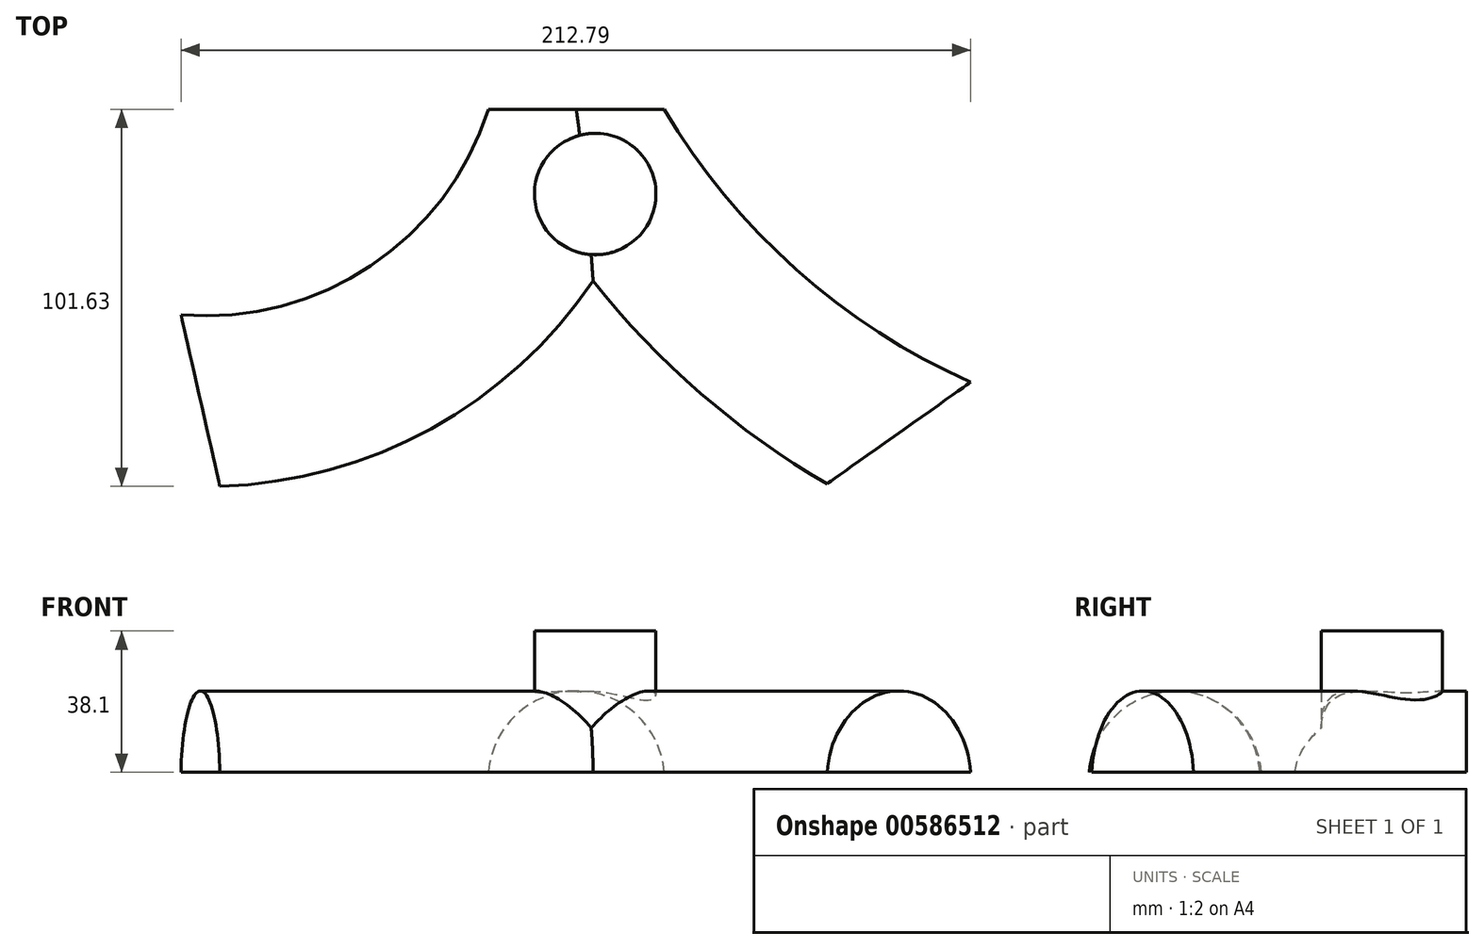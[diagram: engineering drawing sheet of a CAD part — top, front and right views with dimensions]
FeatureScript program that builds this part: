
annotation { "Feature Type Name" : "Feature", "Feature Type Description" : "" }
export const myFeature = defineFeature(function(context is Context, id is Id, definition is map)
    precondition{}
    {
        {
            var Q0;
            Q0=qCreatedBy(makeId("Front.planeOp"),FACE);
            var sketch = newSketch(context, id + "F0", { "sketchPlane" : qUnion([Q0])});
            skArc(sketch, "E0", {"start": v(22.83, 0) * mm, "mid": v(-0.87, 21.9) * mm, "end": v(-24.57, 0) * mm});
            skLineSegment(sketch, "E1", {"start": v(-24.57, 0) * mm, "end": v(22.83, 0) * mm});
            skSolve(sketch);
        }
        {
            var Q0;
            Q0=qCreatedBy(makeId("Top.planeOp"),FACE);
            var sketch = newSketch(context, id + "F1", { "sketchPlane" : qUnion([Q0])});
            skArc(sketch, "E2", {"start": v(-101.98, -79.36) * mm, "mid": v(-37.09, -57.54) * mm, "end": v(0, 0) * mm});
            skSolve(sketch);
        }
        {
            var Q0;
            Q0=qCreatedBy(makeId("Top.planeOp"),FACE);
            var sketch = newSketch(context, id + "F2", { "sketchPlane" : qUnion([Q0])});
            skArc(sketch, "E3", {"start": v(0, 0) * mm, "mid": v(36.64, -50.12) * mm, "end": v(86.76, -86.76) * mm});
            skSolve(sketch);
        }
        {
            var Q0;
            Q0=qCreatedBy(makeId("Top.planeOp"),FACE);
            var sketch = newSketch(context, id + "F3", { "sketchPlane" : qUnion([Q0])});
            skCircle(sketch, "E4", {"center": v(4.22, -22.83) * mm, "radius": 16.37 * mm});
            skSolve(sketch);
        }
        {
            var Q0;
            Q0=makeQuery(id+"F0.imprint","IMPRINT",FACE,{"disambiguationData":[TD([[makeQuery(id+"F0.imprint","IMPRINT",EDGE,{"derivedFrom":sQuery(id+"F0.wireOp",EDGE,"E0")}),1.0]])]});
            var Q1;
            Q1=sQuery(id+"F1.wireOp",EDGE,"E2");
            sweep(context, id + "F4", {"profiles" : qUnion([Q0]), "path" : qUnion([Q1])});
        }
        {
            var Q0;
            Q0=makeQuery(id+"F4.opSweep","CAP_FACE",FACE,{"disambiguationData":[OSD([sQuery(id+"F0.wireOp",EDGE,"E0"),sQuery(id+"F0.wireOp",EDGE,"E1"),sQuery(id+"F1.wireOp",VERTEX,"E2.end")])],"isStart":true});
            var Q1;
            Q1=sQuery(id+"F2.wireOp",EDGE,"E3");
            sweep(context, id + "F5", {"operationType" : NewBodyOperationType.ADD, "profiles" : qUnion([Q0]), "path" : qUnion([Q1])});
        }
        {
            var Q0;
            Q0=makeQuery(id+"F3.imprint","IMPRINT",FACE,{"disambiguationData":[TD([[makeQuery(id+"F3.imprint","IMPRINT",EDGE,{"derivedFrom":sQuery(id+"F3.wireOp",EDGE,"E4")}),1.0]])]});
            var Q1;
            Q1=sQuery(id+"F3.wireOp",EDGE,"E4");
            extrude(context, id + "F6", {"entities" : qUnion([Q0]), "operationType" : NewBodyOperationType.ADD, "surfaceEntities" : qUnion([Q1]), "depth" : 38.1 * mm, "offsetDistance" : 25.4 * mm});
        }
    });
